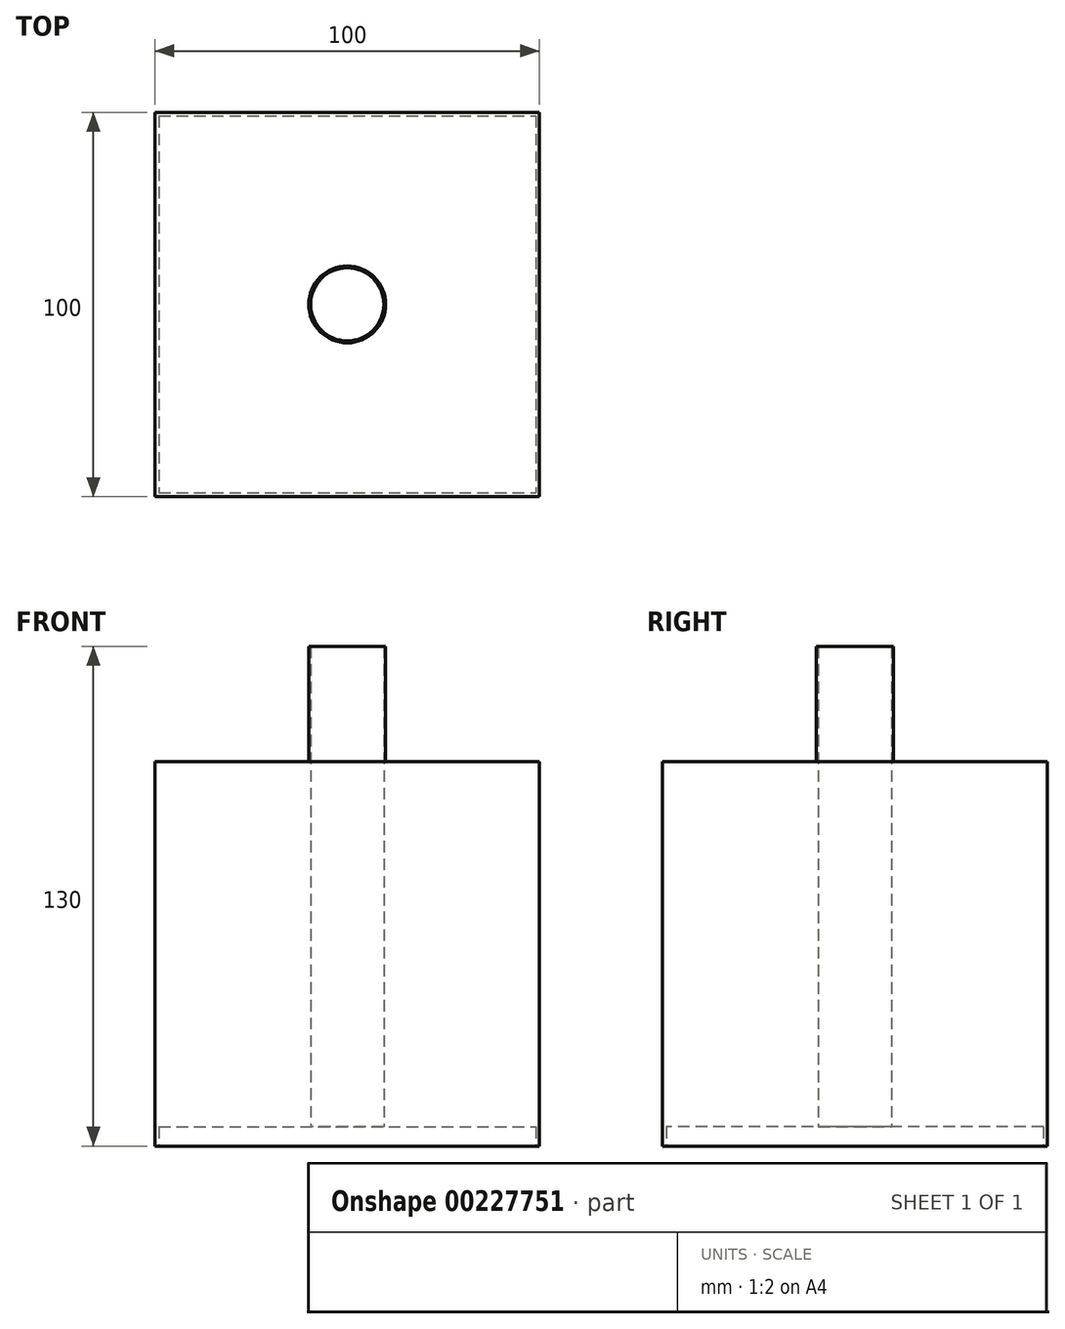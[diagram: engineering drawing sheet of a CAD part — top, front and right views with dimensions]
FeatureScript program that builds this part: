
annotation { "Feature Type Name" : "Feature", "Feature Type Description" : "" }
export const myFeature = defineFeature(function(context is Context, id is Id, definition is map)
    precondition{}
    {
        {
            var Q0;
            Q0=qCreatedBy(makeId("Top.planeOp"),FACE);
            var sketch = newSketch(context, id + "F0", { "sketchPlane" : qUnion([Q0])});
            skLineSegment(sketch, "E0.bottom", {"start": v(-50, 50) * mm, "end": v(50, 50) * mm});
            skLineSegment(sketch, "E0.top", {"start": v(-50, -50) * mm, "end": v(50, -50) * mm});
            skLineSegment(sketch, "E0.left", {"start": v(-50, 50) * mm, "end": v(-50, -50) * mm});
            skLineSegment(sketch, "E0.right", {"start": v(50, 50) * mm, "end": v(50, -50) * mm});
            skSolve(sketch);
        }
        {
            var Q0;
            Q0 = qSketchRegion(id + "F0", true);
            extrude(context, id + "F1", {"entities" : qUnion([Q0]), "oppositeDirection" : true, "depth" : 100 * mm});
        }
        {
            var Q0;
            Q0=qCreatedBy(makeId("Top.planeOp"),FACE);
            var sketch = newSketch(context, id + "F2", { "sketchPlane" : qUnion([Q0])});
            skCircle(sketch, "E1", {"center": v(0, 0) * mm, "radius": 10 * mm});
            skCircle(sketch, "E2", {"center": v(0, 0) * mm, "radius": 9.5 * mm});
            skSolve(sketch);
        }
        {
            var Q0;
            Q0=makeQuery(id+"F2.imprint","IMPRINT",FACE,{"disambiguationData":[TD([[makeQuery(id+"F2.imprint","IMPRINT",EDGE,{"derivedFrom":sQuery(id+"F2.wireOp",EDGE,"E1")}),1.0]])]});
            extrude(context, id + "F3", {"entities" : qUnion([Q0]), "operationType" : NewBodyOperationType.ADD, "depth" : 30 * mm});
        }
        {
            var Q0;
            Q0=makeQuery(id+"F3.boolean.opBoolean","SPLIT",FACE,{"disambiguationData":[TD([makeQuery(id+"F3.opExtrude","SWEPT_FACE",FACE,{"disambiguationData":[OSD([sQuery(id+"F2.wireOp",EDGE,"E2")])]})])],"derivedFrom":makeQuery(id+"F1.opExtrude","CAP_FACE",FACE,{"disambiguationData":[OSD([sQuery(id+"F0.wireOp",EDGE,"E0.bottom"),sQuery(id+"F0.wireOp",EDGE,"E0.top"),sQuery(id+"F0.wireOp",EDGE,"E0.left"),sQuery(id+"F0.wireOp",EDGE,"E0.right")])],"isStart":true})});
            extrude(context, id + "F4", {"entities" : qUnion([Q0]), "operationType" : NewBodyOperationType.REMOVE, "endBound" : BoundingType.UP_TO_NEXT, "oppositeDirection" : true, "depth" : 25 * mm});
        }
        {
            var Q0;
            Q0=makeQuery(id+"F1.opExtrude","CAP_FACE",FACE,{"disambiguationData":[OSD([sQuery(id+"F0.wireOp",EDGE,"E0.bottom"),sQuery(id+"F0.wireOp",EDGE,"E0.top"),sQuery(id+"F0.wireOp",EDGE,"E0.left"),sQuery(id+"F0.wireOp",EDGE,"E0.right")])],"isStart":false});
            var sketch = newSketch(context, id + "F5", { "sketchPlane" : qUnion([Q0])});
            skLineSegment(sketch, "E3.0", {"start": v(-49, -49) * mm, "end": v(49, -49) * mm});
            skLineSegment(sketch, "E3.1", {"start": v(-49, -49) * mm, "end": v(-49, 49) * mm});
            skLineSegment(sketch, "E3.2", {"start": v(-49, 49) * mm, "end": v(49, 49) * mm});
            skLineSegment(sketch, "E3.3", {"start": v(49, -49) * mm, "end": v(49, 49) * mm});
            skSolve(sketch);
        }
        {
            var Q0;
            Q0=makeQuery(id+"F5.imprint","IMPRINT",FACE,{"disambiguationData":[TD([[makeQuery(id+"F5.imprint","IMPRINT",EDGE,{"derivedFrom":makeQuery(id+"F4.boolean.opBoolean","COPY",EDGE,{"derivedFrom":makeQuery(id+"F4.opExtrude","TWEAK_EDGE",EDGE,{"derivedFrom":[makeQuery(id+"F1.opExtrude","CAP_FACE",FACE,{"disambiguationData":[OSD([sQuery(id+"F0.wireOp",EDGE,"E0.bottom"),sQuery(id+"F0.wireOp",EDGE,"E0.top"),sQuery(id+"F0.wireOp",EDGE,"E0.left"),sQuery(id+"F0.wireOp",EDGE,"E0.right")])],"isStart":false}),makeQuery(id+"F3.opExtrude","CAP_EDGE",EDGE,{"disambiguationData":[OSD([sQuery(id+"F2.wireOp",EDGE,"E2")])],"isStart":true})]})})}),1.0]])]});
            var Q1;
            Q1=makeQuery(id+"F5.imprint","IMPRINT",FACE,{"disambiguationData":[TD([[makeQuery(id+"F5.imprint","IMPRINT",EDGE,{"derivedFrom":sQuery(id+"F5.wireOp",EDGE,"E3.0")}),1.0]])]});
            extrude(context, id + "F6", {"entities" : qUnion([Q0, Q1]), "operationType" : NewBodyOperationType.REMOVE, "oppositeDirection" : true, "depth" : 5 * mm});
        }
    });
